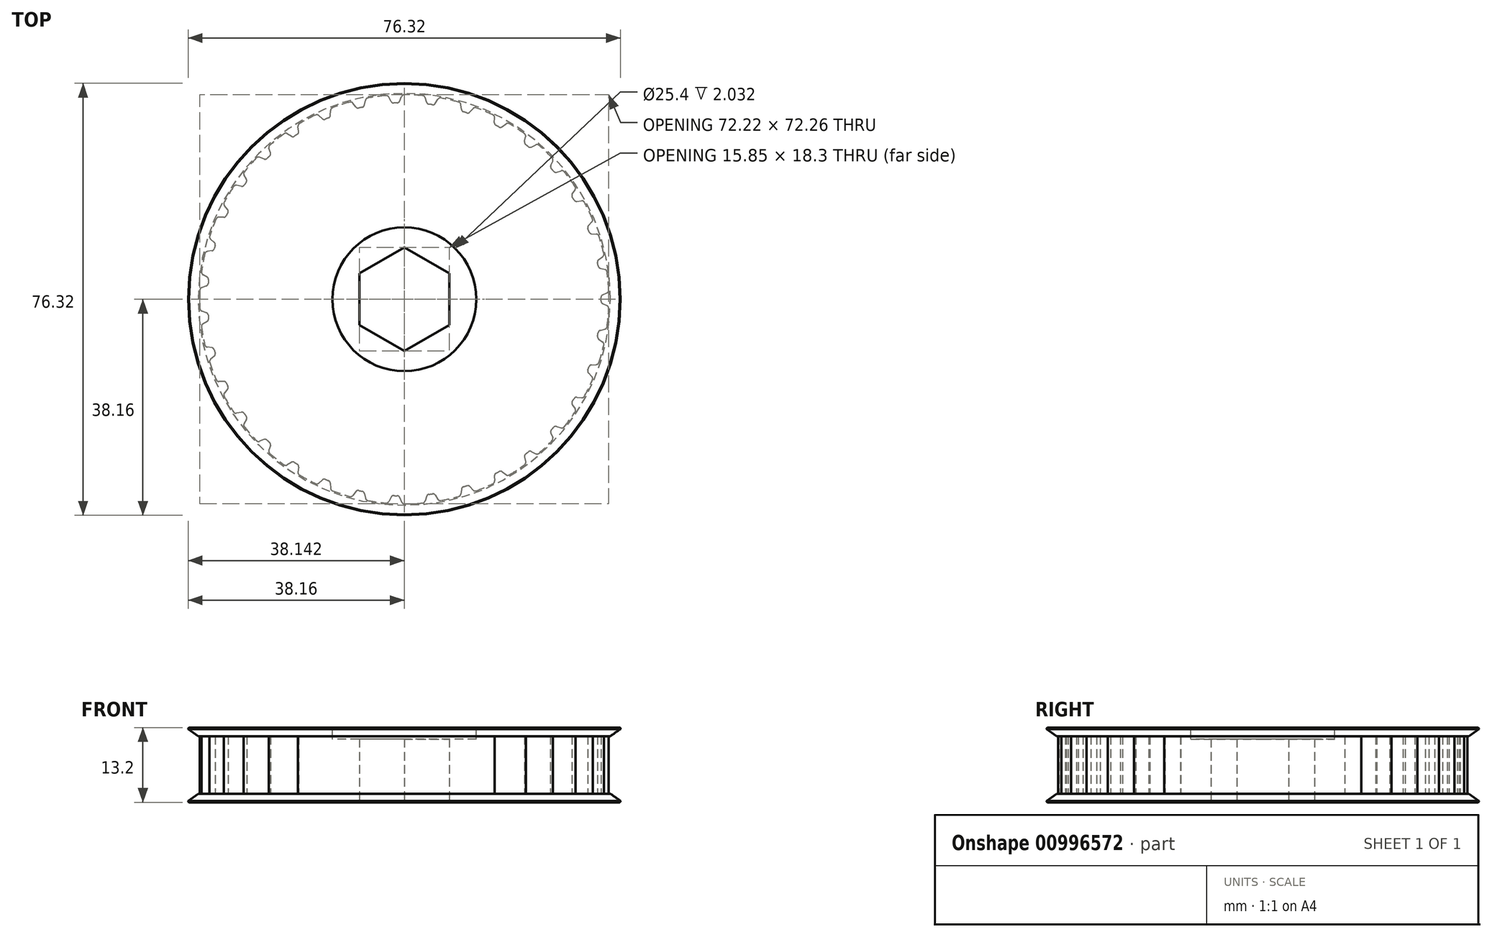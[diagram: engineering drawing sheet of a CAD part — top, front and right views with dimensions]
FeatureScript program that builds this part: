
annotation { "Feature Type Name" : "Feature", "Feature Type Description" : "" }
export const myFeature = defineFeature(function(context is Context, id is Id, definition is map)
    precondition{}
    {
        {
            var Q0;
            Q0=qCreatedBy(makeId("Top.planeOp"),FACE);
            var sketch = newSketch(context, id + "F0", { "sketchPlane" : qUnion([Q0])});
            skCircle(sketch, "E0.cCircle", {"center": v(0, 0) * mm, "radius": 7.92 * mm, "construction": true});
            skLineSegment(sketch, "E0.0", {"start": v(7.92, 4.58) * mm, "end": v(7.92, -4.58) * mm});
            skLineSegment(sketch, "E0.1", {"start": v(7.92, -4.58) * mm, "end": v(0, -9.15) * mm});
            skLineSegment(sketch, "E0.2", {"start": v(0, -9.15) * mm, "end": v(-7.92, -4.58) * mm});
            skLineSegment(sketch, "E0.3", {"start": v(-7.92, -4.58) * mm, "end": v(-7.92, 4.58) * mm});
            skLineSegment(sketch, "E0.4", {"start": v(-7.92, 4.58) * mm, "end": v(0, 9.15) * mm});
            skLineSegment(sketch, "E0.5", {"start": v(0, 9.15) * mm, "end": v(7.92, 4.58) * mm});
            skPoint(sketch, "E0.0.midPoint", {"position": v(7.92, 0) * mm});
            skArc(sketch, "E1", {"start": v(34.73, 0) * mm, "mid": v(34.73, 0.16) * mm, "end": v(34.73, 0.31) * mm});
            skArc(sketch, "E2.MirrorCS", {"start": v(34.73, 0) * mm, "mid": v(34.73, -0.16) * mm, "end": v(34.73, -0.31) * mm});
            skLineSegment(sketch, "E3", {"start": v(35.02, 0.77) * mm, "end": v(35.8, 1.14) * mm});
            skCircle(sketch, "E4", {"center": v(0, 0) * mm, "radius": 36.13 * mm, "construction": true});
            skLineSegment(sketch, "E5.MirrorCS", {"start": v(35.02, -0.77) * mm, "end": v(35.8, -1.14) * mm});
            skLineSegment(sketch, "E6", {"start": v(0, 0) * mm, "end": v(35.93, 3.76) * mm, "construction": true});
            skLineSegment(sketch, "E7", {"start": v(0, 0) * mm, "end": v(36.1, -1.28) * mm, "construction": true});
            skArc(sketch, "E8", {"start": v(36.1, 1.62) * mm, "mid": v(36.03, 2.7) * mm, "end": v(35.93, 3.76) * mm, "construction": true});
            skPoint(sketch, "E9.visualSharp", {"position": v(34.73, 0.63) * mm});
            skArc(sketch, "E9.filletArc", {"start": v(35.02, 0.77) * mm, "mid": v(34.8, 0.59) * mm, "end": v(34.73, 0.31) * mm});
            skPoint(sketch, "E10.visualSharp", {"position": v(34.73, -0.63) * mm});
            skArc(sketch, "E10.filletArc", {"start": v(34.73, -0.31) * mm, "mid": v(34.8, -0.59) * mm, "end": v(35.02, -0.77) * mm});
            skArc(sketch, "E11.MirrorCS", {"start": v(36.1, -1.62) * mm, "mid": v(36.03, -2.7) * mm, "end": v(35.93, -3.76) * mm, "construction": true});
            skPoint(sketch, "E12.visualSharp", {"position": v(36.1, -1.28) * mm});
            skArc(sketch, "E12.filletArc", {"start": v(36.1, -1.62) * mm, "mid": v(36.02, -1.33) * mm, "end": v(35.8, -1.14) * mm});
            skPoint(sketch, "E13.visualSharp", {"position": v(36.1, 1.28) * mm});
            skArc(sketch, "E13.filletArc", {"start": v(35.8, 1.14) * mm, "mid": v(36.02, 1.33) * mm, "end": v(36.1, 1.62) * mm});
            skArc(sketch, "E14.1.0", {"start": v(35.02, 7.5) * mm, "mid": v(35.2, 7.74) * mm, "end": v(35.22, 8.04) * mm});
            skLineSegment(sketch, "E14.1.1", {"start": v(34.32, 7.01) * mm, "end": v(35.02, 7.5) * mm});
            skArc(sketch, "E14.1.2", {"start": v(34.32, 7.01) * mm, "mid": v(34.14, 6.8) * mm, "end": v(34.12, 6.51) * mm});
            skArc(sketch, "E14.1.3", {"start": v(34.17, 6.2) * mm, "mid": v(34.15, 6.36) * mm, "end": v(34.12, 6.51) * mm});
            skArc(sketch, "E14.1.4", {"start": v(34.17, 6.2) * mm, "mid": v(34.2, 6.05) * mm, "end": v(34.23, 5.9) * mm});
            skArc(sketch, "E14.1.5", {"start": v(34.23, 5.9) * mm, "mid": v(34.35, 5.64) * mm, "end": v(34.6, 5.5) * mm});
            skLineSegment(sketch, "E14.1.6", {"start": v(34.6, 5.5) * mm, "end": v(35.43, 5.28) * mm});
            skArc(sketch, "E14.1.7", {"start": v(35.8, 4.85) * mm, "mid": v(35.68, 5.12) * mm, "end": v(35.43, 5.28) * mm});
            skArc(sketch, "E14.2.0", {"start": v(33.12, 13.64) * mm, "mid": v(33.26, 13.9) * mm, "end": v(33.22, 14.2) * mm});
            skLineSegment(sketch, "E14.2.1", {"start": v(32.52, 13.03) * mm, "end": v(33.12, 13.64) * mm});
            skArc(sketch, "E14.2.2", {"start": v(32.52, 13.03) * mm, "mid": v(32.38, 12.78) * mm, "end": v(32.4, 12.5) * mm});
            skArc(sketch, "E14.2.3", {"start": v(32.52, 12.2) * mm, "mid": v(32.46, 12.35) * mm, "end": v(32.4, 12.5) * mm});
            skArc(sketch, "E14.2.4", {"start": v(32.52, 12.2) * mm, "mid": v(32.57, 12.06) * mm, "end": v(32.63, 11.9) * mm});
            skArc(sketch, "E14.2.5", {"start": v(32.63, 11.9) * mm, "mid": v(32.8, 11.68) * mm, "end": v(33.06, 11.58) * mm});
            skLineSegment(sketch, "E14.2.6", {"start": v(33.06, 11.58) * mm, "end": v(33.92, 11.52) * mm});
            skArc(sketch, "E14.2.7", {"start": v(34.36, 11.17) * mm, "mid": v(34.2, 11.4) * mm, "end": v(33.92, 11.52) * mm});
            skArc(sketch, "E14.3.0", {"start": v(30.15, 19.34) * mm, "mid": v(30.24, 19.62) * mm, "end": v(30.15, 19.9) * mm});
            skLineSegment(sketch, "E14.3.1", {"start": v(29.67, 18.62) * mm, "end": v(30.15, 19.34) * mm});
            skArc(sketch, "E14.3.2", {"start": v(29.67, 18.62) * mm, "mid": v(29.58, 18.36) * mm, "end": v(29.65, 18.08) * mm});
            skArc(sketch, "E14.3.3", {"start": v(29.82, 17.81) * mm, "mid": v(29.74, 17.95) * mm, "end": v(29.65, 18.08) * mm});
            skArc(sketch, "E14.3.4", {"start": v(29.82, 17.81) * mm, "mid": v(29.9, 17.68) * mm, "end": v(29.98, 17.54) * mm});
            skArc(sketch, "E14.3.5", {"start": v(29.98, 17.54) * mm, "mid": v(30.18, 17.35) * mm, "end": v(30.46, 17.3) * mm});
            skLineSegment(sketch, "E14.3.6", {"start": v(30.46, 17.3) * mm, "end": v(31.32, 17.39) * mm});
            skArc(sketch, "E14.3.7", {"start": v(31.81, 17.12) * mm, "mid": v(31.6, 17.33) * mm, "end": v(31.32, 17.39) * mm});
            skArc(sketch, "E14.4.0", {"start": v(26.21, 24.4) * mm, "mid": v(26.25, 24.7) * mm, "end": v(26.12, 24.97) * mm});
            skLineSegment(sketch, "E14.4.1", {"start": v(25.86, 23.62) * mm, "end": v(26.21, 24.4) * mm});
            skArc(sketch, "E14.4.2", {"start": v(25.86, 23.62) * mm, "mid": v(25.83, 23.34) * mm, "end": v(25.95, 23.09) * mm});
            skArc(sketch, "E14.4.3", {"start": v(26.16, 22.85) * mm, "mid": v(26.05, 22.97) * mm, "end": v(25.95, 23.09) * mm});
            skArc(sketch, "E14.4.4", {"start": v(26.16, 22.85) * mm, "mid": v(26.26, 22.73) * mm, "end": v(26.36, 22.61) * mm});
            skArc(sketch, "E14.4.5", {"start": v(26.36, 22.61) * mm, "mid": v(26.6, 22.46) * mm, "end": v(26.88, 22.46) * mm});
            skLineSegment(sketch, "E14.4.6", {"start": v(26.88, 22.46) * mm, "end": v(27.7, 22.7) * mm});
            skArc(sketch, "E14.4.7", {"start": v(28.25, 22.53) * mm, "mid": v(28, 22.7) * mm, "end": v(27.7, 22.7) * mm});
            skArc(sketch, "E14.5.0", {"start": v(21.43, 28.7) * mm, "mid": v(21.42, 29) * mm, "end": v(21.24, 29.23) * mm});
            skLineSegment(sketch, "E14.5.1", {"start": v(21.23, 27.86) * mm, "end": v(21.43, 28.7) * mm});
            skArc(sketch, "E14.5.2", {"start": v(21.23, 27.86) * mm, "mid": v(21.25, 27.58) * mm, "end": v(21.4, 27.35) * mm});
            skArc(sketch, "E14.5.3", {"start": v(21.66, 27.16) * mm, "mid": v(21.53, 27.25) * mm, "end": v(21.4, 27.35) * mm});
            skArc(sketch, "E14.5.4", {"start": v(21.66, 27.16) * mm, "mid": v(21.78, 27.06) * mm, "end": v(21.9, 26.96) * mm});
            skArc(sketch, "E14.5.5", {"start": v(21.9, 26.96) * mm, "mid": v(22.16, 26.85) * mm, "end": v(22.44, 26.9) * mm});
            skLineSegment(sketch, "E14.5.6", {"start": v(22.44, 26.9) * mm, "end": v(23.2, 27.28) * mm});
            skArc(sketch, "E14.5.7", {"start": v(23.77, 27.2) * mm, "mid": v(23.5, 27.33) * mm, "end": v(23.2, 27.28) * mm});
            skArc(sketch, "E14.6.0", {"start": v(15.96, 32.06) * mm, "mid": v(15.9, 32.35) * mm, "end": v(15.68, 32.55) * mm});
            skLineSegment(sketch, "E14.6.1", {"start": v(15.92, 31.2) * mm, "end": v(15.96, 32.06) * mm});
            skArc(sketch, "E14.6.2", {"start": v(15.92, 31.2) * mm, "mid": v(15.98, 30.93) * mm, "end": v(16.18, 30.73) * mm});
            skArc(sketch, "E14.6.3", {"start": v(16.46, 30.59) * mm, "mid": v(16.32, 30.66) * mm, "end": v(16.18, 30.73) * mm});
            skArc(sketch, "E14.6.4", {"start": v(16.46, 30.59) * mm, "mid": v(16.6, 30.51) * mm, "end": v(16.73, 30.44) * mm});
            skArc(sketch, "E14.6.5", {"start": v(16.73, 30.44) * mm, "mid": v(17.01, 30.37) * mm, "end": v(17.27, 30.47) * mm});
            skLineSegment(sketch, "E14.6.6", {"start": v(17.27, 30.47) * mm, "end": v(17.96, 30.99) * mm});
            skArc(sketch, "E14.6.7", {"start": v(18.53, 31.02) * mm, "mid": v(18.24, 31.09) * mm, "end": v(17.96, 30.99) * mm});
            skArc(sketch, "E14.7.0", {"start": v(9.98, 34.4) * mm, "mid": v(9.86, 34.67) * mm, "end": v(9.61, 34.83) * mm});
            skLineSegment(sketch, "E14.7.1", {"start": v(10.09, 33.54) * mm, "end": v(9.98, 34.4) * mm});
            skArc(sketch, "E14.7.2", {"start": v(10.09, 33.54) * mm, "mid": v(10.2, 33.29) * mm, "end": v(10.43, 33.13) * mm});
            skArc(sketch, "E14.7.3", {"start": v(10.73, 33.03) * mm, "mid": v(10.58, 33.08) * mm, "end": v(10.43, 33.13) * mm});
            skArc(sketch, "E14.7.4", {"start": v(10.73, 33.03) * mm, "mid": v(10.88, 32.98) * mm, "end": v(11.03, 32.93) * mm});
            skArc(sketch, "E14.7.5", {"start": v(11.03, 32.93) * mm, "mid": v(11.31, 32.92) * mm, "end": v(11.56, 33.07) * mm});
            skLineSegment(sketch, "E14.7.6", {"start": v(11.56, 33.07) * mm, "end": v(12.14, 33.7) * mm});
            skArc(sketch, "E14.7.7", {"start": v(12.7, 33.83) * mm, "mid": v(12.4, 33.85) * mm, "end": v(12.14, 33.7) * mm});
            skArc(sketch, "E14.8.0", {"start": v(3.68, 35.63) * mm, "mid": v(3.51, 35.87) * mm, "end": v(3.24, 35.98) * mm});
            skLineSegment(sketch, "E14.8.1", {"start": v(3.94, 34.8) * mm, "end": v(3.68, 35.63) * mm});
            skArc(sketch, "E14.8.2", {"start": v(3.94, 34.8) * mm, "mid": v(4.1, 34.57) * mm, "end": v(4.35, 34.46) * mm});
            skArc(sketch, "E14.8.3", {"start": v(4.66, 34.42) * mm, "mid": v(4.5, 34.44) * mm, "end": v(4.35, 34.46) * mm});
            skArc(sketch, "E14.8.4", {"start": v(4.66, 34.42) * mm, "mid": v(4.82, 34.4) * mm, "end": v(4.97, 34.37) * mm});
            skArc(sketch, "E14.8.5", {"start": v(4.97, 34.37) * mm, "mid": v(5.25, 34.41) * mm, "end": v(5.47, 34.6) * mm});
            skLineSegment(sketch, "E14.8.6", {"start": v(5.47, 34.6) * mm, "end": v(5.93, 35.32) * mm});
            skArc(sketch, "E14.8.7", {"start": v(6.45, 35.55) * mm, "mid": v(6.16, 35.52) * mm, "end": v(5.93, 35.32) * mm});
            skArc(sketch, "E14.9.0", {"start": v(-2.74, 35.71) * mm, "mid": v(-2.95, 35.92) * mm, "end": v(-3.24, 35.98) * mm});
            skLineSegment(sketch, "E14.9.1", {"start": v(-2.34, 34.95) * mm, "end": v(-2.74, 35.71) * mm});
            skArc(sketch, "E14.9.2", {"start": v(-2.34, 34.95) * mm, "mid": v(-2.15, 34.75) * mm, "end": v(-1.87, 34.68) * mm});
            skArc(sketch, "E14.9.3", {"start": v(-1.56, 34.7) * mm, "mid": v(-1.72, 34.7) * mm, "end": v(-1.87, 34.68) * mm});
            skArc(sketch, "E14.9.4", {"start": v(-1.56, 34.7) * mm, "mid": v(-1.4, 34.7) * mm, "end": v(-1.24, 34.71) * mm});
            skArc(sketch, "E14.9.5", {"start": v(-1.24, 34.71) * mm, "mid": v(-0.98, 34.8) * mm, "end": v(-0.8, 35.02) * mm});
            skLineSegment(sketch, "E14.9.6", {"start": v(-0.8, 35.02) * mm, "end": v(-0.47, 35.82) * mm});
            skArc(sketch, "E14.9.7", {"start": v(0, 36.13) * mm, "mid": v(-0.28, 36.04) * mm, "end": v(-0.47, 35.82) * mm});
            skArc(sketch, "E14.10.0", {"start": v(-9.07, 34.65) * mm, "mid": v(-9.31, 34.82) * mm, "end": v(-9.6, 34.83) * mm});
            skLineSegment(sketch, "E14.10.1", {"start": v(-8.55, 33.97) * mm, "end": v(-9.07, 34.65) * mm});
            skArc(sketch, "E14.10.2", {"start": v(-8.55, 33.97) * mm, "mid": v(-8.32, 33.8) * mm, "end": v(-8.03, 33.8) * mm});
            skArc(sketch, "E14.10.3", {"start": v(-7.73, 33.86) * mm, "mid": v(-7.88, 33.83) * mm, "end": v(-8.03, 33.8) * mm});
            skArc(sketch, "E14.10.4", {"start": v(-7.73, 33.86) * mm, "mid": v(-7.58, 33.9) * mm, "end": v(-7.42, 33.93) * mm});
            skArc(sketch, "E14.10.5", {"start": v(-7.42, 33.93) * mm, "mid": v(-7.18, 34.07) * mm, "end": v(-7.04, 34.31) * mm});
            skLineSegment(sketch, "E14.10.6", {"start": v(-7.04, 34.31) * mm, "end": v(-6.86, 35.16) * mm});
            skArc(sketch, "E14.10.7", {"start": v(-6.45, 35.55) * mm, "mid": v(-6.72, 35.41) * mm, "end": v(-6.86, 35.16) * mm});
            skArc(sketch, "E14.11.0", {"start": v(-15.11, 32.47) * mm, "mid": v(-15.38, 32.6) * mm, "end": v(-15.67, 32.55) * mm});
            skLineSegment(sketch, "E14.11.1", {"start": v(-14.47, 31.9) * mm, "end": v(-15.11, 32.47) * mm});
            skArc(sketch, "E14.11.2", {"start": v(-14.47, 31.9) * mm, "mid": v(-14.22, 31.78) * mm, "end": v(-13.94, 31.81) * mm});
            skArc(sketch, "E14.11.3", {"start": v(-13.65, 31.94) * mm, "mid": v(-13.8, 31.88) * mm, "end": v(-13.94, 31.81) * mm});
            skArc(sketch, "E14.11.4", {"start": v(-13.65, 31.94) * mm, "mid": v(-13.5, 32) * mm, "end": v(-13.36, 32.06) * mm});
            skArc(sketch, "E14.11.5", {"start": v(-13.36, 32.06) * mm, "mid": v(-13.14, 32.24) * mm, "end": v(-13.05, 32.5) * mm});
            skLineSegment(sketch, "E14.11.6", {"start": v(-13.05, 32.5) * mm, "end": v(-13.03, 33.37) * mm});
            skArc(sketch, "E14.11.7", {"start": v(-12.7, 33.83) * mm, "mid": v(-12.93, 33.65) * mm, "end": v(-13.03, 33.37) * mm});
            skArc(sketch, "E14.12.0", {"start": v(-20.67, 29.25) * mm, "mid": v(-20.96, 29.33) * mm, "end": v(-21.23, 29.23) * mm});
            skLineSegment(sketch, "E14.12.1", {"start": v(-19.94, 28.8) * mm, "end": v(-20.67, 29.25) * mm});
            skArc(sketch, "E14.12.2", {"start": v(-19.94, 28.8) * mm, "mid": v(-19.66, 28.73) * mm, "end": v(-19.4, 28.81) * mm});
            skArc(sketch, "E14.12.3", {"start": v(-19.13, 28.99) * mm, "mid": v(-19.27, 28.9) * mm, "end": v(-19.4, 28.81) * mm});
            skArc(sketch, "E14.12.4", {"start": v(-19.13, 28.99) * mm, "mid": v(-19, 29.07) * mm, "end": v(-18.87, 29.16) * mm});
            skArc(sketch, "E14.12.5", {"start": v(-18.87, 29.16) * mm, "mid": v(-18.69, 29.37) * mm, "end": v(-18.65, 29.65) * mm});
            skLineSegment(sketch, "E14.12.6", {"start": v(-18.65, 29.65) * mm, "end": v(-18.77, 30.5) * mm});
            skArc(sketch, "E14.12.7", {"start": v(-18.53, 31.01) * mm, "mid": v(-18.73, 30.8) * mm, "end": v(-18.77, 30.5) * mm});
            skArc(sketch, "E14.13.0", {"start": v(-25.56, 25.1) * mm, "mid": v(-25.86, 25.11) * mm, "end": v(-26.11, 24.97) * mm});
            skLineSegment(sketch, "E14.13.1", {"start": v(-24.76, 24.78) * mm, "end": v(-25.56, 25.1) * mm});
            skArc(sketch, "E14.13.2", {"start": v(-24.76, 24.78) * mm, "mid": v(-24.48, 24.76) * mm, "end": v(-24.23, 24.89) * mm});
            skArc(sketch, "E14.13.3", {"start": v(-24, 25.1) * mm, "mid": v(-24.12, 25) * mm, "end": v(-24.23, 24.89) * mm});
            skArc(sketch, "E14.13.4", {"start": v(-24, 25.1) * mm, "mid": v(-23.89, 25.21) * mm, "end": v(-23.77, 25.32) * mm});
            skArc(sketch, "E14.13.5", {"start": v(-23.77, 25.32) * mm, "mid": v(-23.63, 25.56) * mm, "end": v(-23.64, 25.85) * mm});
            skLineSegment(sketch, "E14.13.6", {"start": v(-23.64, 25.85) * mm, "end": v(-23.92, 26.66) * mm});
            skArc(sketch, "E14.13.7", {"start": v(-23.77, 27.2) * mm, "mid": v(-23.93, 26.96) * mm, "end": v(-23.92, 26.66) * mm});
            skArc(sketch, "E14.14.0", {"start": v(-29.63, 20.12) * mm, "mid": v(-29.92, 20.1) * mm, "end": v(-30.15, 19.9) * mm});
            skLineSegment(sketch, "E14.14.1", {"start": v(-28.79, 19.96) * mm, "end": v(-29.63, 20.12) * mm});
            skArc(sketch, "E14.14.2", {"start": v(-28.79, 19.96) * mm, "mid": v(-28.5, 19.99) * mm, "end": v(-28.28, 20.16) * mm});
            skArc(sketch, "E14.14.3", {"start": v(-28.1, 20.42) * mm, "mid": v(-28.2, 20.29) * mm, "end": v(-28.28, 20.16) * mm});
            skArc(sketch, "E14.14.4", {"start": v(-28.1, 20.42) * mm, "mid": v(-28, 20.54) * mm, "end": v(-27.91, 20.67) * mm});
            skArc(sketch, "E14.14.5", {"start": v(-27.91, 20.67) * mm, "mid": v(-27.82, 20.93) * mm, "end": v(-27.88, 21.2) * mm});
            skLineSegment(sketch, "E14.14.6", {"start": v(-27.88, 21.2) * mm, "end": v(-28.3, 21.96) * mm});
            skArc(sketch, "E14.14.7", {"start": v(-28.25, 22.52) * mm, "mid": v(-28.36, 22.25) * mm, "end": v(-28.3, 21.96) * mm});
            skArc(sketch, "E14.15.0", {"start": v(-32.75, 14.51) * mm, "mid": v(-33.03, 14.43) * mm, "end": v(-33.22, 14.2) * mm});
            skLineSegment(sketch, "E14.15.1", {"start": v(-31.89, 14.5) * mm, "end": v(-32.75, 14.51) * mm});
            skArc(sketch, "E14.15.2", {"start": v(-31.89, 14.5) * mm, "mid": v(-31.62, 14.58) * mm, "end": v(-31.43, 14.79) * mm});
            skArc(sketch, "E14.15.3", {"start": v(-31.3, 15.07) * mm, "mid": v(-31.36, 14.93) * mm, "end": v(-31.43, 14.79) * mm});
            skArc(sketch, "E14.15.4", {"start": v(-31.3, 15.07) * mm, "mid": v(-31.22, 15.21) * mm, "end": v(-31.16, 15.35) * mm});
            skArc(sketch, "E14.15.5", {"start": v(-31.16, 15.35) * mm, "mid": v(-31.1, 15.63) * mm, "end": v(-31.22, 15.89) * mm});
            skLineSegment(sketch, "E14.15.6", {"start": v(-31.22, 15.89) * mm, "end": v(-31.76, 16.56) * mm});
            skArc(sketch, "E14.15.7", {"start": v(-31.82, 17.12) * mm, "mid": v(-31.88, 16.83) * mm, "end": v(-31.76, 16.56) * mm});
            skArc(sketch, "E15", {"start": v(36.1, 1.62) * mm, "mid": v(35.98, 3.24) * mm, "end": v(35.8, 4.85) * mm});
            skArc(sketch, "E16.1.0", {"start": v(35.22, 8.04) * mm, "mid": v(34.83, 9.61) * mm, "end": v(34.36, 11.17) * mm});
            skArc(sketch, "E16.2.0", {"start": v(33.22, 14.2) * mm, "mid": v(32.55, 15.68) * mm, "end": v(31.81, 17.12) * mm});
            skArc(sketch, "E16.3.0", {"start": v(30.15, 19.9) * mm, "mid": v(29.23, 21.24) * mm, "end": v(28.25, 22.53) * mm});
            skArc(sketch, "E16.4.0", {"start": v(26.12, 24.97) * mm, "mid": v(24.97, 26.11) * mm, "end": v(23.77, 27.2) * mm});
            skArc(sketch, "E16.5.0", {"start": v(21.24, 29.23) * mm, "mid": v(19.9, 30.15) * mm, "end": v(18.53, 31.02) * mm});
            skArc(sketch, "E16.6.0", {"start": v(15.68, 32.55) * mm, "mid": v(14.2, 33.22) * mm, "end": v(12.7, 33.83) * mm});
            skArc(sketch, "E16.7.0", {"start": v(9.61, 34.83) * mm, "mid": v(8.04, 35.22) * mm, "end": v(6.45, 35.55) * mm});
            skArc(sketch, "E16.8.0", {"start": v(3.24, 35.98) * mm, "mid": v(1.62, 36.1) * mm, "end": v(0, 36.13) * mm});
            skArc(sketch, "E16.9.0", {"start": v(-3.24, 35.98) * mm, "mid": v(-4.85, 35.8) * mm, "end": v(-6.45, 35.55) * mm});
            skArc(sketch, "E16.10.0", {"start": v(-9.6, 34.83) * mm, "mid": v(-11.16, 34.36) * mm, "end": v(-12.7, 33.83) * mm});
            skArc(sketch, "E16.11.0", {"start": v(-15.67, 32.55) * mm, "mid": v(-17.12, 31.82) * mm, "end": v(-18.53, 31.01) * mm});
            skArc(sketch, "E16.12.0", {"start": v(-21.23, 29.23) * mm, "mid": v(-22.53, 28.25) * mm, "end": v(-23.77, 27.2) * mm});
            skArc(sketch, "E16.13.0", {"start": v(-26.11, 24.97) * mm, "mid": v(-27.2, 23.77) * mm, "end": v(-28.25, 22.52) * mm});
            skArc(sketch, "E16.14.0", {"start": v(-30.15, 19.9) * mm, "mid": v(-31.02, 18.53) * mm, "end": v(-31.82, 17.12) * mm});
            skArc(sketch, "E16.15.0", {"start": v(-33.22, 14.2) * mm, "mid": v(-33.83, 12.7) * mm, "end": v(-34.36, 11.16) * mm});
            skArc(sketch, "E17.2.16.0", {"start": v(-34.81, 8.43) * mm, "mid": v(-35.08, 8.3) * mm, "end": v(-35.22, 8.04) * mm});
            skLineSegment(sketch, "E17.4.16.0", {"start": v(-33.96, 8.57) * mm, "end": v(-34.81, 8.43) * mm});
            skArc(sketch, "E17.7.16.0", {"start": v(-33.96, 8.57) * mm, "mid": v(-33.7, 8.7) * mm, "end": v(-33.56, 8.94) * mm});
            skArc(sketch, "E17.11.16.0", {"start": v(-33.48, 9.24) * mm, "mid": v(-33.52, 9.09) * mm, "end": v(-33.56, 8.94) * mm});
            skArc(sketch, "E17.15.16.0", {"start": v(-33.48, 9.24) * mm, "mid": v(-33.44, 9.4) * mm, "end": v(-33.4, 9.54) * mm});
            skArc(sketch, "E17.19.16.0", {"start": v(-33.4, 9.54) * mm, "mid": v(-33.4, 9.82) * mm, "end": v(-33.55, 10.06) * mm});
            skLineSegment(sketch, "E17.23.16.0", {"start": v(-33.55, 10.06) * mm, "end": v(-34.2, 10.62) * mm});
            skArc(sketch, "E17.26.16.0", {"start": v(-34.36, 11.16) * mm, "mid": v(-34.37, 10.87) * mm, "end": v(-34.2, 10.62) * mm});
            skArc(sketch, "E17.2.17.0", {"start": v(-35.76, 2.08) * mm, "mid": v(-36, 1.9) * mm, "end": v(-36.1, 1.62) * mm});
            skLineSegment(sketch, "E17.4.17.0", {"start": v(-34.95, 2.37) * mm, "end": v(-35.76, 2.08) * mm});
            skArc(sketch, "E17.7.17.0", {"start": v(-34.95, 2.37) * mm, "mid": v(-34.72, 2.54) * mm, "end": v(-34.62, 2.8) * mm});
            skArc(sketch, "E17.11.17.0", {"start": v(-34.6, 3.11) * mm, "mid": v(-34.6, 2.96) * mm, "end": v(-34.62, 2.8) * mm});
            skArc(sketch, "E17.15.17.0", {"start": v(-34.6, 3.11) * mm, "mid": v(-34.58, 3.27) * mm, "end": v(-34.56, 3.43) * mm});
            skArc(sketch, "E17.19.17.0", {"start": v(-34.56, 3.43) * mm, "mid": v(-34.62, 3.7) * mm, "end": v(-34.8, 3.9) * mm});
            skLineSegment(sketch, "E17.23.17.0", {"start": v(-34.8, 3.9) * mm, "end": v(-35.55, 4.34) * mm});
            skArc(sketch, "E17.26.17.0", {"start": v(-35.8, 4.85) * mm, "mid": v(-35.76, 4.56) * mm, "end": v(-35.55, 4.34) * mm});
            skArc(sketch, "E17.2.18.0", {"start": v(-35.55, -4.34) * mm, "mid": v(-35.76, -4.56) * mm, "end": v(-35.8, -4.85) * mm});
            skLineSegment(sketch, "E17.4.18.0", {"start": v(-34.8, -3.9) * mm, "end": v(-35.55, -4.34) * mm});
            skArc(sketch, "E17.7.18.0", {"start": v(-34.8, -3.9) * mm, "mid": v(-34.62, -3.7) * mm, "end": v(-34.56, -3.43) * mm});
            skArc(sketch, "E17.11.18.0", {"start": v(-34.6, -3.11) * mm, "mid": v(-34.58, -3.27) * mm, "end": v(-34.56, -3.43) * mm});
            skArc(sketch, "E17.15.18.0", {"start": v(-34.6, -3.11) * mm, "mid": v(-34.6, -2.96) * mm, "end": v(-34.62, -2.8) * mm});
            skArc(sketch, "E17.19.18.0", {"start": v(-34.62, -2.8) * mm, "mid": v(-34.72, -2.54) * mm, "end": v(-34.95, -2.37) * mm});
            skLineSegment(sketch, "E17.23.18.0", {"start": v(-34.95, -2.37) * mm, "end": v(-35.76, -2.08) * mm});
            skArc(sketch, "E17.26.18.0", {"start": v(-36.1, -1.62) * mm, "mid": v(-36, -1.9) * mm, "end": v(-35.76, -2.08) * mm});
            skArc(sketch, "E17.2.19.0", {"start": v(-34.2, -10.62) * mm, "mid": v(-34.37, -10.87) * mm, "end": v(-34.36, -11.16) * mm});
            skLineSegment(sketch, "E17.4.19.0", {"start": v(-33.55, -10.06) * mm, "end": v(-34.2, -10.62) * mm});
            skArc(sketch, "E17.7.19.0", {"start": v(-33.55, -10.06) * mm, "mid": v(-33.4, -9.82) * mm, "end": v(-33.4, -9.54) * mm});
            skArc(sketch, "E17.11.19.0", {"start": v(-33.48, -9.24) * mm, "mid": v(-33.44, -9.4) * mm, "end": v(-33.4, -9.54) * mm});
            skArc(sketch, "E17.15.19.0", {"start": v(-33.48, -9.24) * mm, "mid": v(-33.52, -9.09) * mm, "end": v(-33.56, -8.94) * mm});
            skArc(sketch, "E17.19.19.0", {"start": v(-33.56, -8.94) * mm, "mid": v(-33.7, -8.7) * mm, "end": v(-33.96, -8.57) * mm});
            skLineSegment(sketch, "E17.23.19.0", {"start": v(-33.96, -8.57) * mm, "end": v(-34.81, -8.43) * mm});
            skArc(sketch, "E17.26.19.0", {"start": v(-35.22, -8.04) * mm, "mid": v(-35.08, -8.3) * mm, "end": v(-34.81, -8.43) * mm});
            skArc(sketch, "E18.1.16.0", {"start": v(-35.22, 8.04) * mm, "mid": v(-35.55, 6.45) * mm, "end": v(-35.8, 4.85) * mm});
            skArc(sketch, "E18.1.17.0", {"start": v(-36.1, 1.62) * mm, "mid": v(-36.13, 0) * mm, "end": v(-36.1, -1.62) * mm});
            skArc(sketch, "E18.1.18.0", {"start": v(-35.8, -4.85) * mm, "mid": v(-35.55, -6.45) * mm, "end": v(-35.22, -8.04) * mm});
            skArc(sketch, "E18.1.19.0", {"start": v(-34.36, -11.16) * mm, "mid": v(-33.83, -12.7) * mm, "end": v(-33.22, -14.2) * mm});
            skArc(sketch, "E19.1.20.0", {"start": v(-31.82, -17.12) * mm, "mid": v(-31.02, -18.53) * mm, "end": v(-30.15, -19.9) * mm});
            skArc(sketch, "E19.1.21.0", {"start": v(-28.25, -22.52) * mm, "mid": v(-27.2, -23.77) * mm, "end": v(-26.11, -24.97) * mm});
            skArc(sketch, "E19.1.22.0", {"start": v(-23.77, -27.2) * mm, "mid": v(-22.53, -28.25) * mm, "end": v(-21.23, -29.23) * mm});
            skArc(sketch, "E19.1.23.0", {"start": v(-18.53, -31.01) * mm, "mid": v(-17.12, -31.82) * mm, "end": v(-15.67, -32.55) * mm});
            skArc(sketch, "E19.1.24.0", {"start": v(-12.7, -33.83) * mm, "mid": v(-11.16, -34.36) * mm, "end": v(-9.6, -34.83) * mm});
            skArc(sketch, "E20.2.20.0", {"start": v(-31.76, -16.56) * mm, "mid": v(-31.88, -16.83) * mm, "end": v(-31.82, -17.12) * mm});
            skLineSegment(sketch, "E20.4.20.0", {"start": v(-31.22, -15.89) * mm, "end": v(-31.76, -16.56) * mm});
            skArc(sketch, "E20.7.20.0", {"start": v(-31.22, -15.89) * mm, "mid": v(-31.1, -15.63) * mm, "end": v(-31.16, -15.35) * mm});
            skArc(sketch, "E20.11.20.0", {"start": v(-31.3, -15.07) * mm, "mid": v(-31.22, -15.21) * mm, "end": v(-31.16, -15.35) * mm});
            skArc(sketch, "E20.15.20.0", {"start": v(-31.3, -15.07) * mm, "mid": v(-31.36, -14.93) * mm, "end": v(-31.43, -14.79) * mm});
            skArc(sketch, "E20.19.20.0", {"start": v(-31.43, -14.79) * mm, "mid": v(-31.62, -14.58) * mm, "end": v(-31.89, -14.5) * mm});
            skLineSegment(sketch, "E20.23.20.0", {"start": v(-31.89, -14.5) * mm, "end": v(-32.75, -14.51) * mm});
            skArc(sketch, "E20.26.20.0", {"start": v(-33.22, -14.2) * mm, "mid": v(-33.03, -14.43) * mm, "end": v(-32.75, -14.51) * mm});
            skArc(sketch, "E20.2.21.0", {"start": v(-28.3, -21.96) * mm, "mid": v(-28.36, -22.25) * mm, "end": v(-28.25, -22.52) * mm});
            skLineSegment(sketch, "E20.4.21.0", {"start": v(-27.88, -21.2) * mm, "end": v(-28.3, -21.96) * mm});
            skArc(sketch, "E20.7.21.0", {"start": v(-27.88, -21.2) * mm, "mid": v(-27.82, -20.93) * mm, "end": v(-27.91, -20.67) * mm});
            skArc(sketch, "E20.11.21.0", {"start": v(-28.1, -20.42) * mm, "mid": v(-28, -20.54) * mm, "end": v(-27.91, -20.67) * mm});
            skArc(sketch, "E20.15.21.0", {"start": v(-28.1, -20.42) * mm, "mid": v(-28.2, -20.29) * mm, "end": v(-28.28, -20.16) * mm});
            skArc(sketch, "E20.19.21.0", {"start": v(-28.28, -20.16) * mm, "mid": v(-28.5, -19.99) * mm, "end": v(-28.79, -19.96) * mm});
            skLineSegment(sketch, "E20.23.21.0", {"start": v(-28.79, -19.96) * mm, "end": v(-29.63, -20.12) * mm});
            skArc(sketch, "E20.26.21.0", {"start": v(-30.15, -19.9) * mm, "mid": v(-29.92, -20.1) * mm, "end": v(-29.63, -20.12) * mm});
            skArc(sketch, "E20.2.22.0", {"start": v(-23.92, -26.66) * mm, "mid": v(-23.93, -26.96) * mm, "end": v(-23.77, -27.2) * mm});
            skLineSegment(sketch, "E20.4.22.0", {"start": v(-23.64, -25.85) * mm, "end": v(-23.92, -26.66) * mm});
            skArc(sketch, "E20.7.22.0", {"start": v(-23.64, -25.85) * mm, "mid": v(-23.63, -25.56) * mm, "end": v(-23.77, -25.32) * mm});
            skArc(sketch, "E20.11.22.0", {"start": v(-24, -25.1) * mm, "mid": v(-23.89, -25.21) * mm, "end": v(-23.77, -25.32) * mm});
            skArc(sketch, "E20.15.22.0", {"start": v(-24, -25.1) * mm, "mid": v(-24.12, -25) * mm, "end": v(-24.23, -24.89) * mm});
            skArc(sketch, "E20.19.22.0", {"start": v(-24.23, -24.89) * mm, "mid": v(-24.48, -24.76) * mm, "end": v(-24.76, -24.78) * mm});
            skLineSegment(sketch, "E20.23.22.0", {"start": v(-24.76, -24.78) * mm, "end": v(-25.56, -25.1) * mm});
            skArc(sketch, "E20.26.22.0", {"start": v(-26.11, -24.97) * mm, "mid": v(-25.86, -25.11) * mm, "end": v(-25.56, -25.1) * mm});
            skArc(sketch, "E20.2.23.0", {"start": v(-18.77, -30.5) * mm, "mid": v(-18.73, -30.8) * mm, "end": v(-18.53, -31.01) * mm});
            skLineSegment(sketch, "E20.4.23.0", {"start": v(-18.65, -29.65) * mm, "end": v(-18.77, -30.5) * mm});
            skArc(sketch, "E20.7.23.0", {"start": v(-18.65, -29.65) * mm, "mid": v(-18.69, -29.37) * mm, "end": v(-18.87, -29.16) * mm});
            skArc(sketch, "E20.11.23.0", {"start": v(-19.13, -28.99) * mm, "mid": v(-19, -29.07) * mm, "end": v(-18.87, -29.16) * mm});
            skArc(sketch, "E20.15.23.0", {"start": v(-19.13, -28.99) * mm, "mid": v(-19.27, -28.9) * mm, "end": v(-19.4, -28.81) * mm});
            skArc(sketch, "E20.19.23.0", {"start": v(-19.4, -28.81) * mm, "mid": v(-19.66, -28.73) * mm, "end": v(-19.94, -28.8) * mm});
            skLineSegment(sketch, "E20.23.23.0", {"start": v(-19.94, -28.8) * mm, "end": v(-20.67, -29.25) * mm});
            skArc(sketch, "E20.26.23.0", {"start": v(-21.23, -29.23) * mm, "mid": v(-20.96, -29.33) * mm, "end": v(-20.67, -29.25) * mm});
            skArc(sketch, "E20.2.24.0", {"start": v(-13.03, -33.37) * mm, "mid": v(-12.93, -33.65) * mm, "end": v(-12.7, -33.83) * mm});
            skLineSegment(sketch, "E20.4.24.0", {"start": v(-13.05, -32.5) * mm, "end": v(-13.03, -33.37) * mm});
            skArc(sketch, "E20.7.24.0", {"start": v(-13.05, -32.5) * mm, "mid": v(-13.14, -32.24) * mm, "end": v(-13.36, -32.06) * mm});
            skArc(sketch, "E20.11.24.0", {"start": v(-13.65, -31.94) * mm, "mid": v(-13.5, -32) * mm, "end": v(-13.36, -32.06) * mm});
            skArc(sketch, "E20.15.24.0", {"start": v(-13.65, -31.94) * mm, "mid": v(-13.8, -31.88) * mm, "end": v(-13.94, -31.81) * mm});
            skArc(sketch, "E20.19.24.0", {"start": v(-13.94, -31.81) * mm, "mid": v(-14.22, -31.78) * mm, "end": v(-14.47, -31.9) * mm});
            skLineSegment(sketch, "E20.23.24.0", {"start": v(-14.47, -31.9) * mm, "end": v(-15.11, -32.47) * mm});
            skArc(sketch, "E20.26.24.0", {"start": v(-15.67, -32.55) * mm, "mid": v(-15.38, -32.6) * mm, "end": v(-15.11, -32.47) * mm});
            skArc(sketch, "E21.1.25.0", {"start": v(-6.45, -35.55) * mm, "mid": v(-4.85, -35.8) * mm, "end": v(-3.24, -35.98) * mm});
            skArc(sketch, "E21.1.26.0", {"start": v(0, -36.13) * mm, "mid": v(1.62, -36.1) * mm, "end": v(3.24, -35.98) * mm});
            skArc(sketch, "E21.1.27.0", {"start": v(6.45, -35.55) * mm, "mid": v(8.04, -35.22) * mm, "end": v(9.61, -34.83) * mm});
            skArc(sketch, "E21.1.28.0", {"start": v(12.7, -33.83) * mm, "mid": v(14.2, -33.22) * mm, "end": v(15.68, -32.55) * mm});
            skArc(sketch, "E21.1.29.0", {"start": v(18.53, -31.02) * mm, "mid": v(19.9, -30.15) * mm, "end": v(21.24, -29.23) * mm});
            skArc(sketch, "E22.2.25.0", {"start": v(-6.86, -35.16) * mm, "mid": v(-6.72, -35.41) * mm, "end": v(-6.45, -35.55) * mm});
            skLineSegment(sketch, "E22.4.25.0", {"start": v(-7.04, -34.31) * mm, "end": v(-6.86, -35.16) * mm});
            skArc(sketch, "E22.7.25.0", {"start": v(-7.04, -34.31) * mm, "mid": v(-7.18, -34.07) * mm, "end": v(-7.42, -33.93) * mm});
            skArc(sketch, "E22.11.25.0", {"start": v(-7.73, -33.86) * mm, "mid": v(-7.58, -33.9) * mm, "end": v(-7.42, -33.93) * mm});
            skArc(sketch, "E22.15.25.0", {"start": v(-7.73, -33.86) * mm, "mid": v(-7.88, -33.83) * mm, "end": v(-8.03, -33.8) * mm});
            skArc(sketch, "E22.19.25.0", {"start": v(-8.03, -33.8) * mm, "mid": v(-8.32, -33.8) * mm, "end": v(-8.55, -33.97) * mm});
            skLineSegment(sketch, "E22.23.25.0", {"start": v(-8.55, -33.97) * mm, "end": v(-9.07, -34.65) * mm});
            skArc(sketch, "E22.26.25.0", {"start": v(-9.6, -34.83) * mm, "mid": v(-9.31, -34.82) * mm, "end": v(-9.07, -34.65) * mm});
            skArc(sketch, "E22.2.26.0", {"start": v(-0.47, -35.82) * mm, "mid": v(-0.28, -36.04) * mm, "end": v(0, -36.13) * mm});
            skLineSegment(sketch, "E22.4.26.0", {"start": v(-0.8, -35.02) * mm, "end": v(-0.47, -35.82) * mm});
            skArc(sketch, "E22.7.26.0", {"start": v(-0.8, -35.02) * mm, "mid": v(-0.98, -34.8) * mm, "end": v(-1.24, -34.71) * mm});
            skArc(sketch, "E22.11.26.0", {"start": v(-1.56, -34.7) * mm, "mid": v(-1.4, -34.7) * mm, "end": v(-1.24, -34.71) * mm});
            skArc(sketch, "E22.15.26.0", {"start": v(-1.56, -34.7) * mm, "mid": v(-1.72, -34.7) * mm, "end": v(-1.87, -34.68) * mm});
            skArc(sketch, "E22.19.26.0", {"start": v(-1.87, -34.68) * mm, "mid": v(-2.15, -34.75) * mm, "end": v(-2.34, -34.95) * mm});
            skLineSegment(sketch, "E22.23.26.0", {"start": v(-2.34, -34.95) * mm, "end": v(-2.74, -35.71) * mm});
            skArc(sketch, "E22.26.26.0", {"start": v(-3.24, -35.98) * mm, "mid": v(-2.95, -35.92) * mm, "end": v(-2.74, -35.71) * mm});
            skArc(sketch, "E22.2.27.0", {"start": v(5.93, -35.32) * mm, "mid": v(6.16, -35.52) * mm, "end": v(6.45, -35.55) * mm});
            skLineSegment(sketch, "E22.4.27.0", {"start": v(5.47, -34.6) * mm, "end": v(5.93, -35.32) * mm});
            skArc(sketch, "E22.7.27.0", {"start": v(5.47, -34.6) * mm, "mid": v(5.25, -34.41) * mm, "end": v(4.97, -34.37) * mm});
            skArc(sketch, "E22.11.27.0", {"start": v(4.66, -34.42) * mm, "mid": v(4.82, -34.4) * mm, "end": v(4.97, -34.37) * mm});
            skArc(sketch, "E22.15.27.0", {"start": v(4.66, -34.42) * mm, "mid": v(4.5, -34.44) * mm, "end": v(4.35, -34.46) * mm});
            skArc(sketch, "E22.19.27.0", {"start": v(4.35, -34.46) * mm, "mid": v(4.1, -34.57) * mm, "end": v(3.94, -34.8) * mm});
            skLineSegment(sketch, "E22.23.27.0", {"start": v(3.94, -34.8) * mm, "end": v(3.68, -35.63) * mm});
            skArc(sketch, "E22.26.27.0", {"start": v(3.24, -35.98) * mm, "mid": v(3.51, -35.87) * mm, "end": v(3.68, -35.63) * mm});
            skArc(sketch, "E22.2.28.0", {"start": v(12.14, -33.7) * mm, "mid": v(12.4, -33.85) * mm, "end": v(12.7, -33.83) * mm});
            skLineSegment(sketch, "E22.4.28.0", {"start": v(11.56, -33.07) * mm, "end": v(12.14, -33.7) * mm});
            skArc(sketch, "E22.7.28.0", {"start": v(11.56, -33.07) * mm, "mid": v(11.31, -32.92) * mm, "end": v(11.03, -32.93) * mm});
            skArc(sketch, "E22.11.28.0", {"start": v(10.73, -33.03) * mm, "mid": v(10.88, -32.98) * mm, "end": v(11.03, -32.93) * mm});
            skArc(sketch, "E22.15.28.0", {"start": v(10.73, -33.03) * mm, "mid": v(10.58, -33.08) * mm, "end": v(10.43, -33.13) * mm});
            skArc(sketch, "E22.19.28.0", {"start": v(10.43, -33.13) * mm, "mid": v(10.2, -33.29) * mm, "end": v(10.09, -33.54) * mm});
            skLineSegment(sketch, "E22.23.28.0", {"start": v(10.09, -33.54) * mm, "end": v(9.98, -34.4) * mm});
            skArc(sketch, "E22.26.28.0", {"start": v(9.61, -34.83) * mm, "mid": v(9.86, -34.67) * mm, "end": v(9.98, -34.4) * mm});
            skArc(sketch, "E22.2.29.0", {"start": v(17.96, -30.99) * mm, "mid": v(18.24, -31.09) * mm, "end": v(18.53, -31.02) * mm});
            skLineSegment(sketch, "E22.4.29.0", {"start": v(17.27, -30.47) * mm, "end": v(17.96, -30.99) * mm});
            skArc(sketch, "E22.7.29.0", {"start": v(17.27, -30.47) * mm, "mid": v(17.01, -30.37) * mm, "end": v(16.73, -30.44) * mm});
            skArc(sketch, "E22.11.29.0", {"start": v(16.46, -30.59) * mm, "mid": v(16.6, -30.51) * mm, "end": v(16.73, -30.44) * mm});
            skArc(sketch, "E22.15.29.0", {"start": v(16.46, -30.59) * mm, "mid": v(16.32, -30.66) * mm, "end": v(16.18, -30.73) * mm});
            skArc(sketch, "E22.19.29.0", {"start": v(16.18, -30.73) * mm, "mid": v(15.98, -30.93) * mm, "end": v(15.92, -31.2) * mm});
            skLineSegment(sketch, "E22.23.29.0", {"start": v(15.92, -31.2) * mm, "end": v(15.96, -32.06) * mm});
            skArc(sketch, "E22.26.29.0", {"start": v(15.68, -32.55) * mm, "mid": v(15.9, -32.35) * mm, "end": v(15.96, -32.06) * mm});
            skArc(sketch, "E23.2.30.0", {"start": v(23.2, -27.28) * mm, "mid": v(23.5, -27.33) * mm, "end": v(23.77, -27.2) * mm});
            skLineSegment(sketch, "E23.4.30.0", {"start": v(22.44, -26.9) * mm, "end": v(23.2, -27.28) * mm});
            skArc(sketch, "E23.7.30.0", {"start": v(22.44, -26.9) * mm, "mid": v(22.16, -26.85) * mm, "end": v(21.9, -26.96) * mm});
            skArc(sketch, "E23.11.30.0", {"start": v(21.66, -27.16) * mm, "mid": v(21.78, -27.06) * mm, "end": v(21.9, -26.96) * mm});
            skArc(sketch, "E23.15.30.0", {"start": v(21.66, -27.16) * mm, "mid": v(21.53, -27.25) * mm, "end": v(21.4, -27.35) * mm});
            skArc(sketch, "E23.19.30.0", {"start": v(21.4, -27.35) * mm, "mid": v(21.25, -27.58) * mm, "end": v(21.23, -27.86) * mm});
            skLineSegment(sketch, "E23.23.30.0", {"start": v(21.23, -27.86) * mm, "end": v(21.43, -28.7) * mm});
            skArc(sketch, "E23.26.30.0", {"start": v(21.24, -29.23) * mm, "mid": v(21.42, -29) * mm, "end": v(21.43, -28.7) * mm});
            skArc(sketch, "E23.2.31.0", {"start": v(27.7, -22.7) * mm, "mid": v(28, -22.7) * mm, "end": v(28.25, -22.53) * mm});
            skLineSegment(sketch, "E23.4.31.0", {"start": v(26.88, -22.46) * mm, "end": v(27.7, -22.7) * mm});
            skArc(sketch, "E23.7.31.0", {"start": v(26.88, -22.46) * mm, "mid": v(26.6, -22.46) * mm, "end": v(26.36, -22.61) * mm});
            skArc(sketch, "E23.11.31.0", {"start": v(26.16, -22.85) * mm, "mid": v(26.26, -22.73) * mm, "end": v(26.36, -22.61) * mm});
            skArc(sketch, "E23.15.31.0", {"start": v(26.16, -22.85) * mm, "mid": v(26.05, -22.97) * mm, "end": v(25.95, -23.09) * mm});
            skArc(sketch, "E23.19.31.0", {"start": v(25.95, -23.09) * mm, "mid": v(25.83, -23.34) * mm, "end": v(25.86, -23.62) * mm});
            skLineSegment(sketch, "E23.23.31.0", {"start": v(25.86, -23.62) * mm, "end": v(26.21, -24.4) * mm});
            skArc(sketch, "E23.26.31.0", {"start": v(26.12, -24.97) * mm, "mid": v(26.25, -24.7) * mm, "end": v(26.21, -24.4) * mm});
            skArc(sketch, "E23.2.32.0", {"start": v(31.32, -17.39) * mm, "mid": v(31.6, -17.33) * mm, "end": v(31.81, -17.12) * mm});
            skLineSegment(sketch, "E23.4.32.0", {"start": v(30.46, -17.3) * mm, "end": v(31.32, -17.39) * mm});
            skArc(sketch, "E23.7.32.0", {"start": v(30.46, -17.3) * mm, "mid": v(30.18, -17.35) * mm, "end": v(29.98, -17.54) * mm});
            skArc(sketch, "E23.11.32.0", {"start": v(29.82, -17.81) * mm, "mid": v(29.9, -17.68) * mm, "end": v(29.98, -17.54) * mm});
            skArc(sketch, "E23.15.32.0", {"start": v(29.82, -17.81) * mm, "mid": v(29.74, -17.95) * mm, "end": v(29.65, -18.08) * mm});
            skArc(sketch, "E23.19.32.0", {"start": v(29.65, -18.08) * mm, "mid": v(29.58, -18.36) * mm, "end": v(29.67, -18.62) * mm});
            skLineSegment(sketch, "E23.23.32.0", {"start": v(29.67, -18.62) * mm, "end": v(30.15, -19.34) * mm});
            skArc(sketch, "E23.26.32.0", {"start": v(30.15, -19.9) * mm, "mid": v(30.24, -19.62) * mm, "end": v(30.15, -19.34) * mm});
            skArc(sketch, "E23.2.33.0", {"start": v(33.92, -11.52) * mm, "mid": v(34.2, -11.4) * mm, "end": v(34.36, -11.17) * mm});
            skLineSegment(sketch, "E23.4.33.0", {"start": v(33.06, -11.58) * mm, "end": v(33.92, -11.52) * mm});
            skArc(sketch, "E23.7.33.0", {"start": v(33.06, -11.58) * mm, "mid": v(32.8, -11.68) * mm, "end": v(32.63, -11.9) * mm});
            skArc(sketch, "E23.11.33.0", {"start": v(32.52, -12.2) * mm, "mid": v(32.57, -12.06) * mm, "end": v(32.63, -11.9) * mm});
            skArc(sketch, "E23.15.33.0", {"start": v(32.52, -12.2) * mm, "mid": v(32.46, -12.35) * mm, "end": v(32.4, -12.5) * mm});
            skArc(sketch, "E23.19.33.0", {"start": v(32.4, -12.5) * mm, "mid": v(32.38, -12.78) * mm, "end": v(32.52, -13.03) * mm});
            skLineSegment(sketch, "E23.23.33.0", {"start": v(32.52, -13.03) * mm, "end": v(33.12, -13.64) * mm});
            skArc(sketch, "E23.26.33.0", {"start": v(33.22, -14.2) * mm, "mid": v(33.26, -13.9) * mm, "end": v(33.12, -13.64) * mm});
            skArc(sketch, "E23.2.34.0", {"start": v(35.43, -5.28) * mm, "mid": v(35.68, -5.12) * mm, "end": v(35.8, -4.85) * mm});
            skLineSegment(sketch, "E23.4.34.0", {"start": v(34.6, -5.5) * mm, "end": v(35.43, -5.28) * mm});
            skArc(sketch, "E23.7.34.0", {"start": v(34.6, -5.5) * mm, "mid": v(34.35, -5.64) * mm, "end": v(34.23, -5.9) * mm});
            skArc(sketch, "E23.11.34.0", {"start": v(34.17, -6.2) * mm, "mid": v(34.2, -6.05) * mm, "end": v(34.23, -5.9) * mm});
            skArc(sketch, "E23.15.34.0", {"start": v(34.17, -6.2) * mm, "mid": v(34.15, -6.36) * mm, "end": v(34.12, -6.51) * mm});
            skArc(sketch, "E23.19.34.0", {"start": v(34.12, -6.51) * mm, "mid": v(34.14, -6.8) * mm, "end": v(34.32, -7.01) * mm});
            skLineSegment(sketch, "E23.23.34.0", {"start": v(34.32, -7.01) * mm, "end": v(35.02, -7.5) * mm});
            skArc(sketch, "E23.26.34.0", {"start": v(35.22, -8.04) * mm, "mid": v(35.2, -7.74) * mm, "end": v(35.02, -7.5) * mm});
            skArc(sketch, "E24.1.30.0", {"start": v(23.77, -27.2) * mm, "mid": v(24.97, -26.11) * mm, "end": v(26.12, -24.97) * mm});
            skArc(sketch, "E24.1.31.0", {"start": v(28.25, -22.53) * mm, "mid": v(29.23, -21.24) * mm, "end": v(30.15, -19.9) * mm});
            skArc(sketch, "E24.1.32.0", {"start": v(31.81, -17.12) * mm, "mid": v(32.55, -15.68) * mm, "end": v(33.22, -14.2) * mm});
            skArc(sketch, "E24.1.33.0", {"start": v(34.36, -11.17) * mm, "mid": v(34.83, -9.61) * mm, "end": v(35.22, -8.04) * mm});
            skArc(sketch, "E24.1.34.0", {"start": v(35.8, -4.85) * mm, "mid": v(35.98, -3.24) * mm, "end": v(36.1, -1.62) * mm});
            skSolve(sketch);
        }
        {
            var Q0;
            Q0=makeQuery(id+"F0.imprint","IMPRINT",FACE,{"disambiguationData":[TD([[makeQuery(id+"F0.imprint","IMPRINT",EDGE,{"derivedFrom":sQuery(id+"F0.wireOp",EDGE,"E0.0")}),1.0]])]});
            extrude(context, id + "F1", {"entities" : qUnion([Q0]), "depth" : 5.08 * mm, "hasSecondDirection" : true, "secondDirectionOppositeDirection" : true, "secondDirectionDepth" : 5.08 * mm});
        }
        {
            var Q0;
            Q0=makeQuery(id+"F1.opExtrude","CAP_FACE",FACE,{"disambiguationData":[OSD([sQuery(id+"F0.wireOp",EDGE,"E0.0"),sQuery(id+"F0.wireOp",EDGE,"E0.1"),sQuery(id+"F0.wireOp",EDGE,"E0.2"),sQuery(id+"F0.wireOp",EDGE,"E0.3"),sQuery(id+"F0.wireOp",EDGE,"E0.4"),sQuery(id+"F0.wireOp",EDGE,"E0.5"),sQuery(id+"F0.wireOp",EDGE,"E1"),sQuery(id+"F0.wireOp",EDGE,"E2.MirrorCS"),sQuery(id+"F0.wireOp",EDGE,"E3"),sQuery(id+"F0.wireOp",EDGE,"E5.MirrorCS"),sQuery(id+"F0.wireOp",EDGE,"E9.filletArc"),sQuery(id+"F0.wireOp",EDGE,"E10.filletArc"),sQuery(id+"F0.wireOp",EDGE,"E12.filletArc"),sQuery(id+"F0.wireOp",EDGE,"E13.filletArc"),sQuery(id+"F0.wireOp",EDGE,"E14.1.0"),sQuery(id+"F0.wireOp",EDGE,"E14.1.1"),sQuery(id+"F0.wireOp",EDGE,"E14.1.2"),sQuery(id+"F0.wireOp",EDGE,"E14.1.3"),sQuery(id+"F0.wireOp",EDGE,"E14.1.4"),sQuery(id+"F0.wireOp",EDGE,"E14.1.5"),sQuery(id+"F0.wireOp",EDGE,"E14.1.6"),sQuery(id+"F0.wireOp",EDGE,"E14.1.7"),sQuery(id+"F0.wireOp",EDGE,"E14.2.0"),sQuery(id+"F0.wireOp",EDGE,"E14.2.1"),sQuery(id+"F0.wireOp",EDGE,"E14.2.2"),sQuery(id+"F0.wireOp",EDGE,"E14.2.3"),sQuery(id+"F0.wireOp",EDGE,"E14.2.4"),sQuery(id+"F0.wireOp",EDGE,"E14.2.5"),sQuery(id+"F0.wireOp",EDGE,"E14.2.6"),sQuery(id+"F0.wireOp",EDGE,"E14.2.7"),sQuery(id+"F0.wireOp",EDGE,"E14.3.0"),sQuery(id+"F0.wireOp",EDGE,"E14.3.1"),sQuery(id+"F0.wireOp",EDGE,"E14.3.2"),sQuery(id+"F0.wireOp",EDGE,"E14.3.3"),sQuery(id+"F0.wireOp",EDGE,"E14.3.4"),sQuery(id+"F0.wireOp",EDGE,"E14.3.5"),sQuery(id+"F0.wireOp",EDGE,"E14.3.6"),sQuery(id+"F0.wireOp",EDGE,"E14.3.7"),sQuery(id+"F0.wireOp",EDGE,"E14.4.0"),sQuery(id+"F0.wireOp",EDGE,"E14.4.1"),sQuery(id+"F0.wireOp",EDGE,"E14.4.2"),sQuery(id+"F0.wireOp",EDGE,"E14.4.3"),sQuery(id+"F0.wireOp",EDGE,"E14.4.4"),sQuery(id+"F0.wireOp",EDGE,"E14.4.5"),sQuery(id+"F0.wireOp",EDGE,"E14.4.6"),sQuery(id+"F0.wireOp",EDGE,"E14.4.7"),sQuery(id+"F0.wireOp",EDGE,"E14.5.0"),sQuery(id+"F0.wireOp",EDGE,"E14.5.1"),sQuery(id+"F0.wireOp",EDGE,"E14.5.2"),sQuery(id+"F0.wireOp",EDGE,"E14.5.3"),sQuery(id+"F0.wireOp",EDGE,"E14.5.4"),sQuery(id+"F0.wireOp",EDGE,"E14.5.5"),sQuery(id+"F0.wireOp",EDGE,"E14.5.6"),sQuery(id+"F0.wireOp",EDGE,"E14.5.7"),sQuery(id+"F0.wireOp",EDGE,"E14.6.0"),sQuery(id+"F0.wireOp",EDGE,"E14.6.1"),sQuery(id+"F0.wireOp",EDGE,"E14.6.2"),sQuery(id+"F0.wireOp",EDGE,"E14.6.3"),sQuery(id+"F0.wireOp",EDGE,"E14.6.4"),sQuery(id+"F0.wireOp",EDGE,"E14.6.5"),sQuery(id+"F0.wireOp",EDGE,"E14.6.6"),sQuery(id+"F0.wireOp",EDGE,"E14.6.7"),sQuery(id+"F0.wireOp",EDGE,"E14.7.0"),sQuery(id+"F0.wireOp",EDGE,"E14.7.1"),sQuery(id+"F0.wireOp",EDGE,"E14.7.2"),sQuery(id+"F0.wireOp",EDGE,"E14.7.3"),sQuery(id+"F0.wireOp",EDGE,"E14.7.4"),sQuery(id+"F0.wireOp",EDGE,"E14.7.5"),sQuery(id+"F0.wireOp",EDGE,"E14.7.6"),sQuery(id+"F0.wireOp",EDGE,"E14.7.7"),sQuery(id+"F0.wireOp",EDGE,"E14.8.0"),sQuery(id+"F0.wireOp",EDGE,"E14.8.1"),sQuery(id+"F0.wireOp",EDGE,"E14.8.2"),sQuery(id+"F0.wireOp",EDGE,"E14.8.3"),sQuery(id+"F0.wireOp",EDGE,"E14.8.4"),sQuery(id+"F0.wireOp",EDGE,"E14.8.5"),sQuery(id+"F0.wireOp",EDGE,"E14.8.6"),sQuery(id+"F0.wireOp",EDGE,"E14.8.7"),sQuery(id+"F0.wireOp",EDGE,"E14.9.0"),sQuery(id+"F0.wireOp",EDGE,"E14.9.1"),sQuery(id+"F0.wireOp",EDGE,"E14.9.2"),sQuery(id+"F0.wireOp",EDGE,"E14.9.3"),sQuery(id+"F0.wireOp",EDGE,"E14.9.4"),sQuery(id+"F0.wireOp",EDGE,"E14.9.5"),sQuery(id+"F0.wireOp",EDGE,"E14.9.6"),sQuery(id+"F0.wireOp",EDGE,"E14.9.7"),sQuery(id+"F0.wireOp",EDGE,"E14.10.0"),sQuery(id+"F0.wireOp",EDGE,"E14.10.1"),sQuery(id+"F0.wireOp",EDGE,"E14.10.2"),sQuery(id+"F0.wireOp",EDGE,"E14.10.3"),sQuery(id+"F0.wireOp",EDGE,"E14.10.4"),sQuery(id+"F0.wireOp",EDGE,"E14.10.5"),sQuery(id+"F0.wireOp",EDGE,"E14.10.6"),sQuery(id+"F0.wireOp",EDGE,"E14.10.7"),sQuery(id+"F0.wireOp",EDGE,"E14.11.0"),sQuery(id+"F0.wireOp",EDGE,"E14.11.1"),sQuery(id+"F0.wireOp",EDGE,"E14.11.2"),sQuery(id+"F0.wireOp",EDGE,"E14.11.3"),sQuery(id+"F0.wireOp",EDGE,"E14.11.4"),sQuery(id+"F0.wireOp",EDGE,"E14.11.5"),sQuery(id+"F0.wireOp",EDGE,"E14.11.6"),sQuery(id+"F0.wireOp",EDGE,"E14.11.7"),sQuery(id+"F0.wireOp",EDGE,"E14.12.0"),sQuery(id+"F0.wireOp",EDGE,"E14.12.1"),sQuery(id+"F0.wireOp",EDGE,"E14.12.2"),sQuery(id+"F0.wireOp",EDGE,"E14.12.3"),sQuery(id+"F0.wireOp",EDGE,"E14.12.4"),sQuery(id+"F0.wireOp",EDGE,"E14.12.5"),sQuery(id+"F0.wireOp",EDGE,"E14.12.6"),sQuery(id+"F0.wireOp",EDGE,"E14.12.7"),sQuery(id+"F0.wireOp",EDGE,"E14.13.0"),sQuery(id+"F0.wireOp",EDGE,"E14.13.1"),sQuery(id+"F0.wireOp",EDGE,"E14.13.2"),sQuery(id+"F0.wireOp",EDGE,"E14.13.3"),sQuery(id+"F0.wireOp",EDGE,"E14.13.4"),sQuery(id+"F0.wireOp",EDGE,"E14.13.5"),sQuery(id+"F0.wireOp",EDGE,"E14.13.6"),sQuery(id+"F0.wireOp",EDGE,"E14.13.7"),sQuery(id+"F0.wireOp",EDGE,"E14.14.0"),sQuery(id+"F0.wireOp",EDGE,"E14.14.1"),sQuery(id+"F0.wireOp",EDGE,"E14.14.2"),sQuery(id+"F0.wireOp",EDGE,"E14.14.3"),sQuery(id+"F0.wireOp",EDGE,"E14.14.4"),sQuery(id+"F0.wireOp",EDGE,"E14.14.5"),sQuery(id+"F0.wireOp",EDGE,"E14.14.6"),sQuery(id+"F0.wireOp",EDGE,"E14.14.7"),sQuery(id+"F0.wireOp",EDGE,"E14.15.0"),sQuery(id+"F0.wireOp",EDGE,"E14.15.1"),sQuery(id+"F0.wireOp",EDGE,"E14.15.2"),sQuery(id+"F0.wireOp",EDGE,"E14.15.3"),sQuery(id+"F0.wireOp",EDGE,"E14.15.4"),sQuery(id+"F0.wireOp",EDGE,"E14.15.5"),sQuery(id+"F0.wireOp",EDGE,"E14.15.6"),sQuery(id+"F0.wireOp",EDGE,"E14.15.7"),sQuery(id+"F0.wireOp",EDGE,"E14.16.0"),sQuery(id+"F0.wireOp",EDGE,"E14.16.1"),sQuery(id+"F0.wireOp",EDGE,"E14.16.2"),sQuery(id+"F0.wireOp",EDGE,"E14.16.3"),sQuery(id+"F0.wireOp",EDGE,"E14.16.4"),sQuery(id+"F0.wireOp",EDGE,"E14.16.5"),sQuery(id+"F0.wireOp",EDGE,"E14.16.6"),sQuery(id+"F0.wireOp",EDGE,"E14.16.7"),sQuery(id+"F0.wireOp",EDGE,"E14.17.0"),sQuery(id+"F0.wireOp",EDGE,"E14.17.1"),sQuery(id+"F0.wireOp",EDGE,"E14.17.2"),sQuery(id+"F0.wireOp",EDGE,"E14.17.3"),sQuery(id+"F0.wireOp",EDGE,"E14.17.4"),sQuery(id+"F0.wireOp",EDGE,"E14.17.5"),sQuery(id+"F0.wireOp",EDGE,"E14.17.6"),sQuery(id+"F0.wireOp",EDGE,"E14.17.7"),sQuery(id+"F0.wireOp",EDGE,"E14.18.0"),sQuery(id+"F0.wireOp",EDGE,"E14.18.1"),sQuery(id+"F0.wireOp",EDGE,"E14.18.2"),sQuery(id+"F0.wireOp",EDGE,"E14.18.3"),sQuery(id+"F0.wireOp",EDGE,"E14.18.4"),sQuery(id+"F0.wireOp",EDGE,"E14.18.5"),sQuery(id+"F0.wireOp",EDGE,"E14.18.6"),sQuery(id+"F0.wireOp",EDGE,"E14.18.7"),sQuery(id+"F0.wireOp",EDGE,"E14.19.0"),sQuery(id+"F0.wireOp",EDGE,"E14.19.1"),sQuery(id+"F0.wireOp",EDGE,"E14.19.2"),sQuery(id+"F0.wireOp",EDGE,"E14.19.3"),sQuery(id+"F0.wireOp",EDGE,"E14.19.4"),sQuery(id+"F0.wireOp",EDGE,"E14.19.5"),sQuery(id+"F0.wireOp",EDGE,"E14.19.6"),sQuery(id+"F0.wireOp",EDGE,"E14.19.7"),sQuery(id+"F0.wireOp",EDGE,"E14.20.0"),sQuery(id+"F0.wireOp",EDGE,"E14.20.1"),sQuery(id+"F0.wireOp",EDGE,"E14.20.2"),sQuery(id+"F0.wireOp",EDGE,"E14.20.3"),sQuery(id+"F0.wireOp",EDGE,"E14.20.4"),sQuery(id+"F0.wireOp",EDGE,"E14.20.5"),sQuery(id+"F0.wireOp",EDGE,"E14.20.6"),sQuery(id+"F0.wireOp",EDGE,"E14.20.7"),sQuery(id+"F0.wireOp",EDGE,"E14.21.0"),sQuery(id+"F0.wireOp",EDGE,"E14.21.1"),sQuery(id+"F0.wireOp",EDGE,"E14.21.2"),sQuery(id+"F0.wireOp",EDGE,"E14.21.3"),sQuery(id+"F0.wireOp",EDGE,"E14.21.4"),sQuery(id+"F0.wireOp",EDGE,"E14.21.5"),sQuery(id+"F0.wireOp",EDGE,"E14.21.6"),sQuery(id+"F0.wireOp",EDGE,"E14.21.7"),sQuery(id+"F0.wireOp",EDGE,"E14.22.0"),sQuery(id+"F0.wireOp",EDGE,"E14.22.1"),sQuery(id+"F0.wireOp",EDGE,"E14.22.2"),sQuery(id+"F0.wireOp",EDGE,"E14.22.3"),sQuery(id+"F0.wireOp",EDGE,"E14.22.4"),sQuery(id+"F0.wireOp",EDGE,"E14.22.5"),sQuery(id+"F0.wireOp",EDGE,"E14.22.6"),sQuery(id+"F0.wireOp",EDGE,"E14.22.7"),sQuery(id+"F0.wireOp",EDGE,"E14.23.0"),sQuery(id+"F0.wireOp",EDGE,"E14.23.1"),sQuery(id+"F0.wireOp",EDGE,"E14.23.2"),sQuery(id+"F0.wireOp",EDGE,"E14.23.3"),sQuery(id+"F0.wireOp",EDGE,"E14.23.4"),sQuery(id+"F0.wireOp",EDGE,"E14.23.5"),sQuery(id+"F0.wireOp",EDGE,"E14.23.6"),sQuery(id+"F0.wireOp",EDGE,"E14.23.7"),sQuery(id+"F0.wireOp",EDGE,"E14.24.0"),sQuery(id+"F0.wireOp",EDGE,"E14.24.1"),sQuery(id+"F0.wireOp",EDGE,"E14.24.2"),sQuery(id+"F0.wireOp",EDGE,"E14.24.3"),sQuery(id+"F0.wireOp",EDGE,"E14.24.4"),sQuery(id+"F0.wireOp",EDGE,"E14.24.5"),sQuery(id+"F0.wireOp",EDGE,"E14.24.6"),sQuery(id+"F0.wireOp",EDGE,"E14.24.7"),sQuery(id+"F0.wireOp",EDGE,"E14.25.0"),sQuery(id+"F0.wireOp",EDGE,"E14.25.1"),sQuery(id+"F0.wireOp",EDGE,"E14.25.2"),sQuery(id+"F0.wireOp",EDGE,"E14.25.3"),sQuery(id+"F0.wireOp",EDGE,"E14.25.4"),sQuery(id+"F0.wireOp",EDGE,"E14.25.5"),sQuery(id+"F0.wireOp",EDGE,"E14.25.6"),sQuery(id+"F0.wireOp",EDGE,"E14.25.7"),sQuery(id+"F0.wireOp",EDGE,"E14.26.0"),sQuery(id+"F0.wireOp",EDGE,"E14.26.1"),sQuery(id+"F0.wireOp",EDGE,"E14.26.2"),sQuery(id+"F0.wireOp",EDGE,"E14.26.3"),sQuery(id+"F0.wireOp",EDGE,"E14.26.4"),sQuery(id+"F0.wireOp",EDGE,"E14.26.5"),sQuery(id+"F0.wireOp",EDGE,"E14.26.6"),sQuery(id+"F0.wireOp",EDGE,"E14.26.7"),sQuery(id+"F0.wireOp",EDGE,"E14.27.0"),sQuery(id+"F0.wireOp",EDGE,"E14.27.1"),sQuery(id+"F0.wireOp",EDGE,"E14.27.2"),sQuery(id+"F0.wireOp",EDGE,"E14.27.3"),sQuery(id+"F0.wireOp",EDGE,"E14.27.4"),sQuery(id+"F0.wireOp",EDGE,"E14.27.5"),sQuery(id+"F0.wireOp",EDGE,"E14.27.6"),sQuery(id+"F0.wireOp",EDGE,"E14.27.7"),sQuery(id+"F0.wireOp",EDGE,"E15"),sQuery(id+"F0.wireOp",EDGE,"E16.1.0"),sQuery(id+"F0.wireOp",EDGE,"E16.2.0"),sQuery(id+"F0.wireOp",EDGE,"E16.3.0"),sQuery(id+"F0.wireOp",EDGE,"E16.4.0"),sQuery(id+"F0.wireOp",EDGE,"E16.5.0"),sQuery(id+"F0.wireOp",EDGE,"E16.6.0"),sQuery(id+"F0.wireOp",EDGE,"E16.7.0"),sQuery(id+"F0.wireOp",EDGE,"E16.8.0"),sQuery(id+"F0.wireOp",EDGE,"E16.9.0"),sQuery(id+"F0.wireOp",EDGE,"E16.10.0"),sQuery(id+"F0.wireOp",EDGE,"E16.11.0"),sQuery(id+"F0.wireOp",EDGE,"E16.12.0"),sQuery(id+"F0.wireOp",EDGE,"E16.13.0"),sQuery(id+"F0.wireOp",EDGE,"E16.14.0"),sQuery(id+"F0.wireOp",EDGE,"E16.15.0"),sQuery(id+"F0.wireOp",EDGE,"E16.16.0"),sQuery(id+"F0.wireOp",EDGE,"E16.17.0"),sQuery(id+"F0.wireOp",EDGE,"E16.18.0"),sQuery(id+"F0.wireOp",EDGE,"E16.19.0"),sQuery(id+"F0.wireOp",EDGE,"E16.20.0"),sQuery(id+"F0.wireOp",EDGE,"E16.21.0"),sQuery(id+"F0.wireOp",EDGE,"E16.22.0"),sQuery(id+"F0.wireOp",EDGE,"E16.23.0"),sQuery(id+"F0.wireOp",EDGE,"E16.24.0"),sQuery(id+"F0.wireOp",EDGE,"E16.25.0"),sQuery(id+"F0.wireOp",EDGE,"E16.26.0"),sQuery(id+"F0.wireOp",EDGE,"E16.27.0")])],"isStart":false});
            var sketch = newSketch(context, id + "F2", { "sketchPlane" : qUnion([Q0])});
            skCircle(sketch, "E25", {"center": v(0, 0) * mm, "radius": 38.16 * mm});
            skLineSegment(sketch, "E26.0", {"start": v(7.92, 4.58) * mm, "end": v(7.92, -4.58) * mm});
            skLineSegment(sketch, "E27.0", {"start": v(0, 9.15) * mm, "end": v(7.92, 4.58) * mm});
            skLineSegment(sketch, "E28.0", {"start": v(-7.92, 4.58) * mm, "end": v(0, 9.15) * mm});
            skLineSegment(sketch, "E29.0", {"start": v(-7.92, -4.58) * mm, "end": v(-7.92, 4.58) * mm});
            skLineSegment(sketch, "E30.0", {"start": v(0, -9.15) * mm, "end": v(-7.92, -4.58) * mm});
            skLineSegment(sketch, "E31.0", {"start": v(7.92, -4.58) * mm, "end": v(0, -9.15) * mm});
            skCircle(sketch, "E32.0", {"center": v(0, 0) * mm, "radius": 36.13 * mm, "construction": true});
            skSolve(sketch);
        }
        {
            var Q0;
            Q0=makeQuery(id+"F2.imprint","IMPRINT",FACE,{"disambiguationData":[TD([[makeQuery(id+"F2.imprint","IMPRINT",EDGE,{"derivedFrom":sQuery(id+"F2.wireOp",EDGE,"E26.0")}),1.0]])]});
            var Q1;
            Q1=makeQuery(id+"F2.imprint","IMPRINT",FACE,{"disambiguationData":[TD([[makeQuery(id+"F2.imprint","IMPRINT",EDGE,{"derivedFrom":sQuery(id+"F2.wireOp",EDGE,"E25")}),1.0]])]});
            extrude(context, id + "F3", {"entities" : qUnion([Q0, Q1]), "depth" : 1.52 * mm});
        }
        {
            var Q0;
            Q0=makeQuery(id+"F3.opExtrude","CAP_EDGE",EDGE,{"disambiguationData":[OSD([sQuery(id+"F2.wireOp",EDGE,"E25")])],"isStart":true});
            chamfer(context, id + "F4", {"entities" : qUnion([Q0]), "chamferType" : ChamferType.TWO_OFFSETS, "width1" : 1.27 * mm, "oppositeDirection" : false, "width2" : 1.78 * mm, "tangentPropagation" : true});
        }
        {
            var Q0;
            Q0=makeQuery(id+"F3.opExtrude","CAP_EDGE",EDGE,{"disambiguationData":[OSD([sQuery(id+"F2.wireOp",EDGE,"E25")])],"isStart":false});
            chamfer(context, id + "F5", {"entities" : qUnion([Q0]), "width" : 0.13 * mm, "tangentPropagation" : true});
        }
        {
            var Q0;
            Q0=makeQuery(id+"F3.opExtrude","SWEPT_BODY",BODY,{"disambiguationData":[OSD([sQuery(id+"F2.wireOp",EDGE,"E25"),sQuery(id+"F2.wireOp",EDGE,"E26.0"),sQuery(id+"F2.wireOp",EDGE,"E27.0"),sQuery(id+"F2.wireOp",EDGE,"E28.0"),sQuery(id+"F2.wireOp",EDGE,"E29.0"),sQuery(id+"F2.wireOp",EDGE,"E30.0"),sQuery(id+"F2.wireOp",EDGE,"E31.0")])]});
            var Q1;
            Q1=qCreatedBy(makeId("Top.planeOp"),FACE);
            mirror(context, id + "F6", {"operationType" : NewBodyOperationType.ADD, "entities" : qUnion([Q0]), "mirrorPlane" : qUnion([Q1])});
        }
        {
            var Q0;
            Q0=makeQuery(id+"F3.opExtrude","CAP_FACE",FACE,{"disambiguationData":[OSD([sQuery(id+"F2.wireOp",EDGE,"E25"),sQuery(id+"F2.wireOp",EDGE,"E26.0"),sQuery(id+"F2.wireOp",EDGE,"E27.0"),sQuery(id+"F2.wireOp",EDGE,"E28.0"),sQuery(id+"F2.wireOp",EDGE,"E29.0"),sQuery(id+"F2.wireOp",EDGE,"E30.0"),sQuery(id+"F2.wireOp",EDGE,"E31.0")])],"isStart":false});
            var sketch = newSketch(context, id + "F7", { "sketchPlane" : qUnion([Q0])});
            skCircle(sketch, "E33", {"center": v(0, 0) * mm, "radius": 12.7 * mm});
            skSolve(sketch);
        }
        {
            var Q0;
            Q0=qSketchRegion(id+"F7",true);
            extrude(context, id + "F8", {"entities" : qUnion([Q0]), "operationType" : NewBodyOperationType.REMOVE, "oppositeDirection" : true, "depth" : 2.03 * mm});
        }
    });
